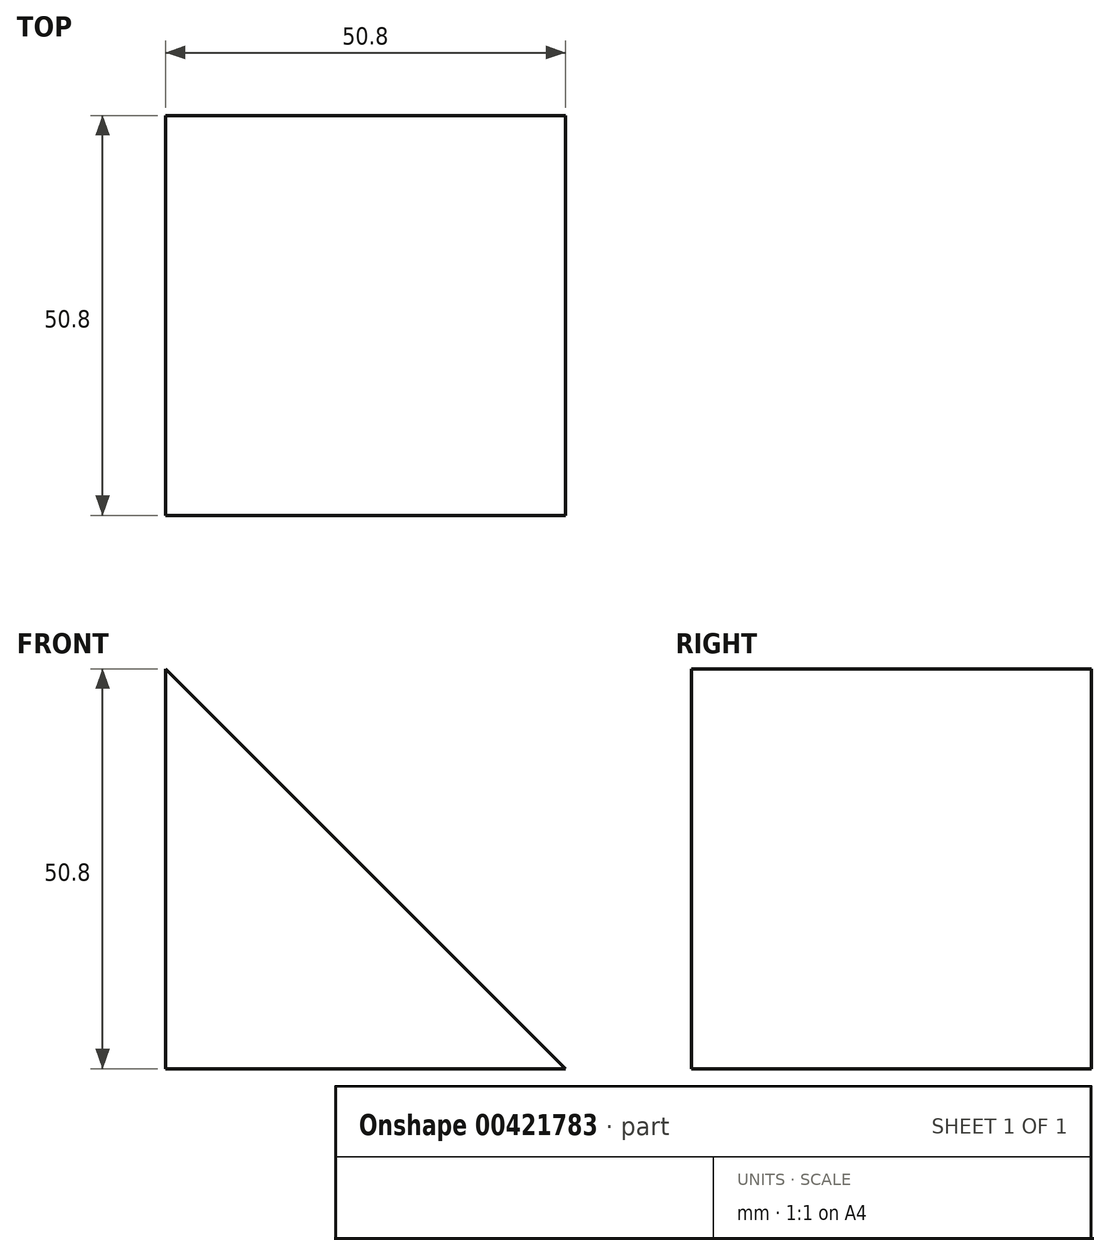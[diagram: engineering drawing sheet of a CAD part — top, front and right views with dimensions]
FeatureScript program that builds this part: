
annotation { "Feature Type Name" : "Feature", "Feature Type Description" : "" }
export const myFeature = defineFeature(function(context is Context, id is Id, definition is map)
    precondition{}
    {
        {
            var Q0;
            Q0=qCreatedBy(makeId("Front.planeOp"),FACE);
            var sketch = newSketch(context, id + "F0", { "sketchPlane" : qUnion([Q0])});
            skLineSegment(sketch, "E0", {"start": v(0, 0) * mm, "end": v(0, 50.8) * mm});
            skLineSegment(sketch, "E1", {"start": v(0, 0) * mm, "end": v(50.8, 0) * mm});
            skLineSegment(sketch, "E2", {"start": v(0, 50.8) * mm, "end": v(50.8, 0) * mm});
            skSolve(sketch);
        }
        {
            var Q0;
            Q0=makeQuery(id+"F0.imprint","IMPRINT",FACE,{"disambiguationData":[TD([[makeQuery(id+"F0.imprint","IMPRINT",EDGE,{"derivedFrom":sQuery(id+"F0.wireOp",EDGE,"E0")}),-1.0]])]});
            extrude(context, id + "F1", {"entities" : qUnion([Q0]), "depth" : 50.8 * mm});
        }
    });
